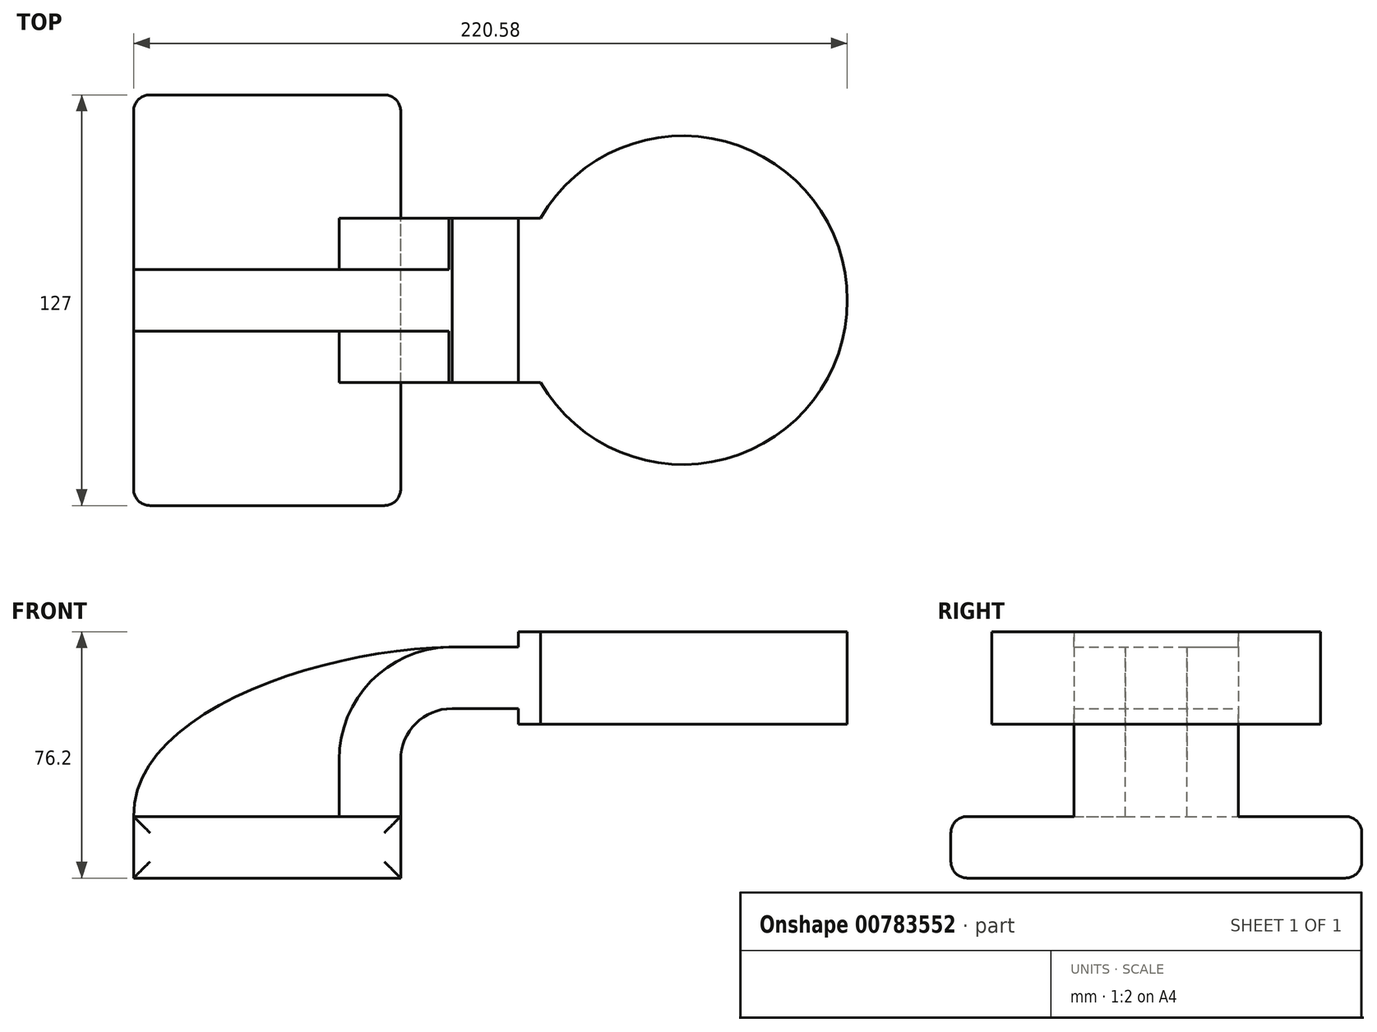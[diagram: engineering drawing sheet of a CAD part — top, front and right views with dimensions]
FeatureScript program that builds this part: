
annotation { "Feature Type Name" : "Feature", "Feature Type Description" : "" }
export const myFeature = defineFeature(function(context is Context, id is Id, definition is map)
    precondition{}
    {
        {
            var Q0;
            Q0=qCreatedBy(makeId("Front.planeOp"),FACE);
            var sketch = newSketch(context, id + "F0", { "sketchPlane" : qUnion([Q0])});
            skLineSegment(sketch, "E0.bottom", {"start": v(41.27, 9.53) * mm, "end": v(-41.28, 9.53) * mm});
            skLineSegment(sketch, "E0.top", {"start": v(41.28, -9.52) * mm, "end": v(-41.27, -9.52) * mm});
            skLineSegment(sketch, "E0.left", {"start": v(41.28, 9.53) * mm, "end": v(41.28, -9.52) * mm});
            skLineSegment(sketch, "E0.right", {"start": v(-41.28, 9.53) * mm, "end": v(-41.28, -9.52) * mm});
            skPoint(sketch, "E0.middle", {"position": v(0, 0) * mm});
            skLineSegment(sketch, "E1.bottom", {"start": v(77.7, 38.1) * mm, "end": v(128.5, 38.1) * mm});
            skLineSegment(sketch, "E1.top", {"start": v(77.7, 66.68) * mm, "end": v(128.5, 66.68) * mm});
            skLineSegment(sketch, "E1.left", {"start": v(77.7, 38.1) * mm, "end": v(77.7, 66.68) * mm});
            skLineSegment(sketch, "E1.right", {"start": v(128.5, 38.1) * mm, "end": v(128.5, 66.68) * mm});
            skPoint(sketch, "E1.middle", {"position": v(103.1, 52.39) * mm});
            skLineSegment(sketch, "E2", {"start": v(41.27, 9.53) * mm, "end": v(41.27, 27) * mm});
            skArc(sketch, "E3", {"start": v(41.27, 27) * mm, "mid": v(45.92, 38.23) * mm, "end": v(57.15, 42.88) * mm});
            skLineSegment(sketch, "E4", {"start": v(57.15, 42.88) * mm, "end": v(103.1, 42.88) * mm});
            skPoint(sketch, "E4.endSnap0", {"position": v(103.1, 38.1) * mm});
            skLineSegment(sketch, "E5.0", {"start": v(57.15, 61.93) * mm, "end": v(103.1, 61.93) * mm});
            skArc(sketch, "E5.1", {"start": v(22.22, 27) * mm, "mid": v(32.45, 51.7) * mm, "end": v(57.15, 61.93) * mm});
            skLineSegment(sketch, "E5.2", {"start": v(22.22, 9.53) * mm, "end": v(22.22, 27) * mm});
            skFitSpline(sketch, "E6", {"points": [v(-41.28, 9.52) * mm, v(57.15, 61.93) * mm], "startDerivative": vector(-1.5, 97.9) * mm, "endDerivative": vector(117.31, 1.22) * mm});
            skSolve(sketch);
        }
        {
            var Q0;
            Q0=makeQuery(id+"F0.imprint","IMPRINT",FACE,{"disambiguationData":[TD([[makeQuery(id+"F0.imprint","IMPRINT",EDGE,{"derivedFrom":sQuery(id+"F0.wireOp",EDGE,"E0.top")}),-1.0]])]});
            extrude(context, id + "F1", {"entities" : qUnion([Q0]), "endBound" : BoundingType.SYMMETRIC, "depth" : 127 * mm, "offsetDistance" : 25.4 * mm});
        }
        {
            var Q0;
            {var subQ1=sQuery(id+"F0.wireOp",EDGE,"E2");Q0=makeQuery(id+"F0.imprint","IMPRINT",FACE,{"disambiguationData":[TD([[makeQuery(id+"F0.imprint","IMPRINT",EDGE,{"derivedFrom":subQ1}),1.0]])]});}
            var Q1;
            {var subQ3=sQuery(id+"F0.wireOp",EDGE,"E1.bottom");Q1=makeQuery(id+"F0.imprint","IMPRINT",FACE,{"disambiguationData":[TD([[makeQuery(id+"F0.imprint","IMPRINT",EDGE,{"derivedFrom":subQ3}),1.0]])]});}
            extrude(context, id + "F2", {"entities" : qUnion([Q0, Q1]), "operationType" : NewBodyOperationType.ADD, "endBound" : BoundingType.SYMMETRIC, "depth" : 50.8 * mm, "offsetDistance" : 25.4 * mm});
        }
        {
            var Q0;
            {var subQ3=sQuery(id+"F0.wireOp",EDGE,"E5.2");Q0=makeQuery(id+"F0.imprint","IMPRINT",FACE,{"disambiguationData":[TD([[makeQuery(id+"F0.imprint","IMPRINT",EDGE,{"derivedFrom":subQ3}),1.0]])]});}
            extrude(context, id + "F3", {"entities" : qUnion([Q0]), "operationType" : NewBodyOperationType.ADD, "endBound" : BoundingType.SYMMETRIC, "depth" : 19.05 * mm, "offsetDistance" : 25.4 * mm});
        }
        {
            var Q0;
            {var subQ3=sQuery(id+"F0.wireOp",EDGE,"E1.bottom");Q0=makeQuery(id+"F0.imprint","IMPRINT",FACE,{"disambiguationData":[TD([[makeQuery(id+"F0.imprint","IMPRINT",EDGE,{"derivedFrom":subQ3}),1.0]])]});}
            var Q1;
            Q1=sQuery(id+"F0.wireOp",EDGE,"E1.right");
            revolve(context, id + "F4", {"operationType" : NewBodyOperationType.ADD, "surfaceOperationType" : NewSurfaceOperationType.NEW, "entities" : qUnion([Q0]), "axis" : qUnion([Q1]), "revolveType" : RevolveType.FULL});
        }
        {
            var Q0;
            Q0=makeQuery(id+"F1.opExtrude","CAP_FACE",FACE,{"disambiguationData":[OSD([sQuery(id+"F0.wireOp",EDGE,"E0.bottom"),sQuery(id+"F0.wireOp",EDGE,"E0.top"),sQuery(id+"F0.wireOp",EDGE,"E0.left"),sQuery(id+"F0.wireOp",EDGE,"E0.right")])],"isStart":true});
            var Q1;
            Q1=makeQuery(id+"F1.opExtrude","CAP_FACE",FACE,{"disambiguationData":[OSD([sQuery(id+"F0.wireOp",EDGE,"E0.bottom"),sQuery(id+"F0.wireOp",EDGE,"E0.top"),sQuery(id+"F0.wireOp",EDGE,"E0.left"),sQuery(id+"F0.wireOp",EDGE,"E0.right")])],"isStart":false});
            fillet(context, id + "F5", {"entities" : qUnion([Q0, Q1]), "radius" : 5.08 * mm, "tangentPropagation" : true, "allowEdgeOverflow" : false});
        }
    });
